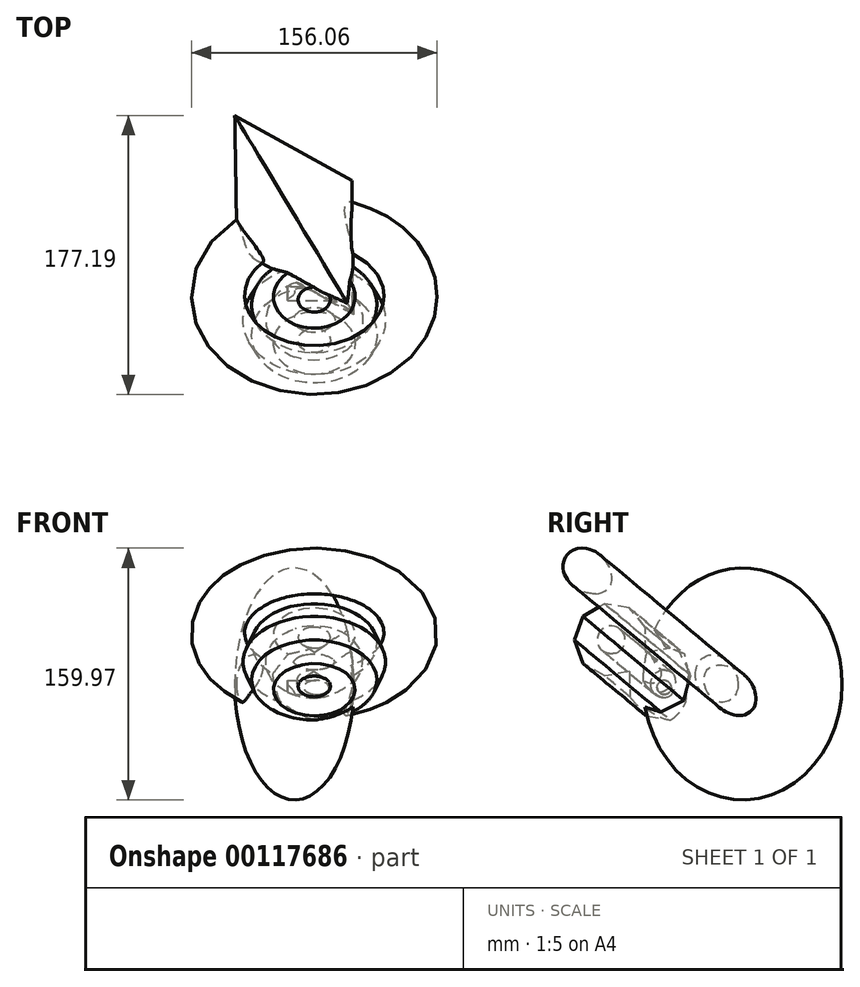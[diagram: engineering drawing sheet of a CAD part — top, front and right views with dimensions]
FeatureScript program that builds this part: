
annotation { "Feature Type Name" : "Feature", "Feature Type Description" : "" }
export const myFeature = defineFeature(function(context is Context, id is Id, definition is map)
    precondition{}
    {
        {
            var Q0;
            Q0=qCreatedBy(makeId("Front.planeOp"),FACE);
            var sketch = newSketch(context, id + "F0", { "sketchPlane" : qUnion([Q0])});
            skLineSegment(sketch, "E0.bottom", {"start": v(16.99, -2.23) * mm, "end": v(-16.99, -2.23) * mm});
            skLineSegment(sketch, "E0.top", {"start": v(16.99, 2.23) * mm, "end": v(-16.99, 2.23) * mm});
            skLineSegment(sketch, "E0.left", {"start": v(16.99, -2.23) * mm, "end": v(16.99, 2.23) * mm});
            skLineSegment(sketch, "E0.right", {"start": v(-16.99, -2.23) * mm, "end": v(-16.99, 2.23) * mm});
            skPoint(sketch, "E0.middle", {"position": v(0, 0) * mm});
            skSolve(sketch);
        }
        {
            var Q0;
            Q0 = qSketchRegion(id + "F0", true);
            var Q1;
            Q1=sQuery(id+"F0.wireOp",EDGE,"E0.bottom");
            revolve(context, id + "F1", {"entities" : qUnion([Q0]), "axis" : qUnion([Q1]), "revolveType" : RevolveType.FULL});
        }
        {
            var Q0;
            Q0=qCreatedBy(makeId("Right.planeOp"),FACE);
            var sketch = newSketch(context, id + "F2", { "sketchPlane" : qUnion([Q0])});
            skCircle(sketch, "E1", {"center": v(0, 0) * mm, "radius": 8.82 * mm});
            skCircle(sketch, "E2.cCircle", {"center": v(0, 0) * mm, "radius": 21.9 * mm, "construction": true});
            skLineSegment(sketch, "E2.0", {"start": v(17.91, -14.9) * mm, "end": v(4.14, -22.94) * mm});
            skLineSegment(sketch, "E2.1", {"start": v(4.14, -22.94) * mm, "end": v(-11.57, -20.23) * mm});
            skLineSegment(sketch, "E2.2", {"start": v(-11.57, -20.23) * mm, "end": v(-21.87, -8.06) * mm});
            skLineSegment(sketch, "E2.3", {"start": v(-21.87, -8.06) * mm, "end": v(-21.93, 7.88) * mm});
            skLineSegment(sketch, "E2.4", {"start": v(-21.93, 7.88) * mm, "end": v(-11.73, 20.14) * mm});
            skLineSegment(sketch, "E2.5", {"start": v(-11.73, 20.14) * mm, "end": v(3.96, 22.97) * mm});
            skLineSegment(sketch, "E2.6", {"start": v(3.96, 22.97) * mm, "end": v(17.8, 15.05) * mm});
            skLineSegment(sketch, "E2.7", {"start": v(17.8, 15.05) * mm, "end": v(23.3, 0.1) * mm});
            skLineSegment(sketch, "E2.8", {"start": v(23.3, 0.1) * mm, "end": v(17.91, -14.9) * mm});
            skPoint(sketch, "E2.0.midPoint", {"position": v(11.03, -18.92) * mm});
            skSolve(sketch);
        }
        {
            var Q0;
            Q0 = qSketchRegion(id + "F2", true);
            var Q1;
            Q1=sQuery(id+"F2.wireOp",EDGE,"E2.4");
            revolve(context, id + "F3", {"operationType" : NewBodyOperationType.ADD, "entities" : qUnion([Q0]), "axis" : qUnion([Q1]), "revolveType" : RevolveType.FULL});
        }
        {
            var Q0;
            Q0=qCreatedBy(makeId("Top.planeOp"),FACE);
            var sketch = newSketch(context, id + "F4", { "sketchPlane" : qUnion([Q0])});
            skCircle(sketch, "E3.cCircle", {"center": v(0, 28.76) * mm, "radius": 24.54 * mm, "construction": true});
            skLineSegment(sketch, "E3.0", {"start": v(25.24, -13.34) * mm, "end": v(-49.08, 27.95) * mm});
            skLineSegment(sketch, "E3.1", {"start": v(-49.08, 27.95) * mm, "end": v(23.84, 71.67) * mm});
            skLineSegment(sketch, "E3.2", {"start": v(23.84, 71.67) * mm, "end": v(25.24, -13.34) * mm});
            skPoint(sketch, "E3.0.midPoint", {"position": v(-11.92, 7.3) * mm});
            skSolve(sketch);
        }
        {
            var Q0;
            Q0 = qSketchRegion(id + "F4", true);
            var Q1;
            Q1=sQuery(id+"F4.wireOp",EDGE,"E3.1");
            revolve(context, id + "F5", {"operationType" : NewBodyOperationType.ADD, "entities" : qUnion([Q0]), "axis" : qUnion([Q1]), "revolveType" : RevolveType.FULL});
        }
        {
            var Q0;
            Q0=qCreatedBy(makeId("Front.planeOp"),FACE);
            var sketch = newSketch(context, id + "F6", { "sketchPlane" : qUnion([Q0])});
            skCircle(sketch, "E4", {"center": v(61.09, 31.14) * mm, "radius": 16.91 * mm});
            skArc(sketch, "E5", {"start": v(47.98, 0) * mm, "mid": v(26.08, 18.92) * mm, "end": v(0, 31.44) * mm});
            skSolve(sketch);
        }
        {
            var Q0;
            Q0 = qSketchRegion(id + "F6", true);
            var Q1;
            Q1=makeQuery(id+"F3.opRevolve","SWEPT_FACE",FACE,{"disambiguationData":[OSD([sQuery(id+"F2.wireOp",EDGE,"E2.7")])]});
            revolve(context, id + "F7", {"operationType" : NewBodyOperationType.ADD, "entities" : qUnion([Q0]), "axis" : qUnion([Q1]), "revolveType" : RevolveType.FULL});
        }
    });
